# Revit family: 60324_PRESTO_Barre coudée à 135° diamètre 32 mm_FR
name_source: partatom
category: Appareils sanitaires
revit_build: Autodesk Revit 2018 (Build: 20190510_1515(x64)
units: mm (PartAtom-declared; Revit-internal decimal feet)

## family parameters
Basée sur le plan de construction = Non
Cote de connecteur circulaire = Utiliser le diamètre
Couper avec des vides une fois chargée = Non
Partagée = Non
Point de calcul de pièce = Non
Toujours verticalement = Oui
Type d'élément = Normal

## types (1)
- 60324 PRESTO Barre coudée à 135° diamètre 32 mm
    Adresse = 7, RUE RACINE - 92542 MONTROUGE CEDEX FRANCE
    Description = Barre de relèvement pour WC. De type presto réf. 60324 ou techniquement équivalent. Avec angle 135°, 3 points de fixation. En inox 304 brossé, de diamètre 32 mm et de longueur 400 x 400 mm. Livrée avec rosaces de finition à clipser.
    Fabricant = LES ROBINETS PRESTO S.A.
    Finition = - Tube acier inox 304
- Platine de fixation inox 304 soudée
- Finition poli satin
    Fonction = Dimensions :
- Diamètre : 32 mm
- Longueur : 400 x 400 mm

Matière et couleur de finition :
- Tube acier inox 304
- Platine de fixation inox 304 soudée
- Finition inox brossé

Livré avec :
- Rosaces en acier inox 304 permettant de dissimuler les vis de fixation

Normes / Agréments :
- Résistance au brouillard salin neutre (NSS) : 200 h selon NF ISO 9227
    Garantie = 3
    Hauteur = 359 mm
    Largeur = 82 mm  [stored 0.269029 ft]
    Lien CCTP = http://www.prestodatashare.com
    Lien fiche produit = http://www.prestodatashare.com
    Lien notice d'utilisation = http://www.prestodatashare.com
    Matériau = PRESTO métal
    Modèle = 60324 PRESTO BARRE 135° INOX Ø32MM
    Profondeur = 758 mm
    Reference = 60324
    URL = http://www.prestodatashare.com
    URL Fabricant = http://www.prestodatashare.com
    Variantes = 60324

note: [stored X ft] marks values corroborated as IEEE doubles in the binary element streams (Revit-internal decimal feet)
